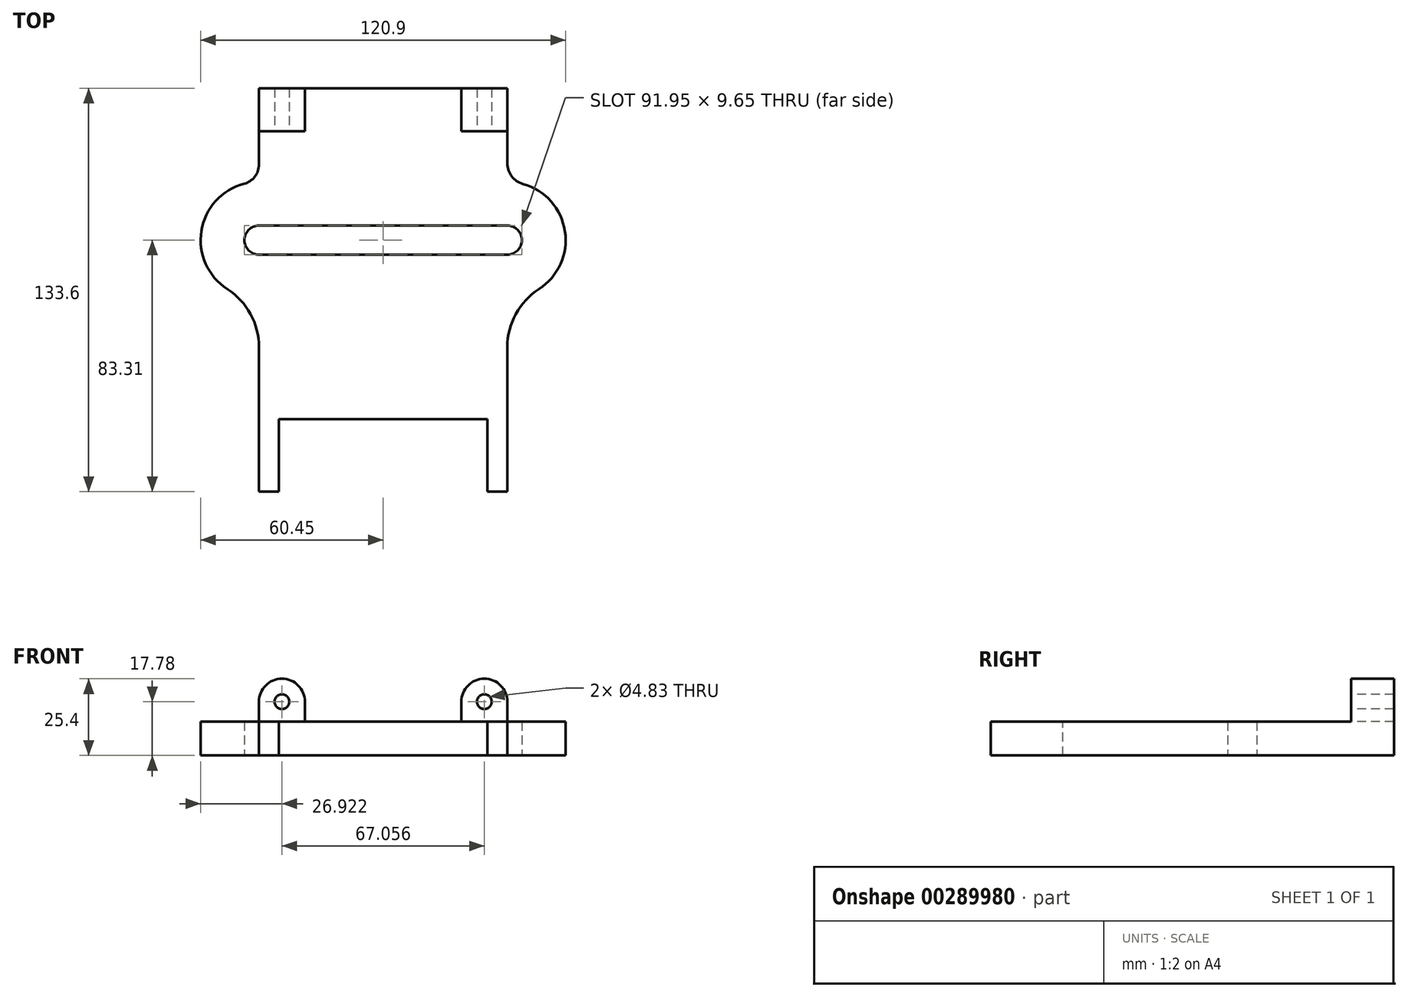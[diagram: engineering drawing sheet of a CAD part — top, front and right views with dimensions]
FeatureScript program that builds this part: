
annotation { "Feature Type Name" : "Feature", "Feature Type Description" : "" }
export const myFeature = defineFeature(function(context is Context, id is Id, definition is map)
    precondition{}
    {
        {
            var Q0;
            Q0=qCreatedBy(makeId("Top.planeOp"),FACE);
            var sketch = newSketch(context, id + "F0", { "sketchPlane" : qUnion([Q0])});
            skLineSegment(sketch, "E0.bottom", {"start": v(41.15, -66.8) * mm, "end": v(-41.15, -66.8) * mm});
            skLineSegment(sketch, "E0.top", {"start": v(41.15, 66.8) * mm, "end": v(-41.15, 66.8) * mm});
            skLineSegment(sketch, "E0.left", {"start": v(41.15, -66.8) * mm, "end": v(41.15, -18.92) * mm});
            skLineSegment(sketch, "E0.right", {"start": v(-41.15, -66.8) * mm, "end": v(-41.15, -18.92) * mm});
            skPoint(sketch, "E0.middle", {"position": v(0, 0) * mm});
            skLineSegment(sketch, "E1.bottom", {"start": v(-36.58, 66.8) * mm, "end": v(36.58, 66.8) * mm});
            skLineSegment(sketch, "E1.top", {"start": v(-36.58, -66.8) * mm, "end": v(36.58, -66.8) * mm});
            skArc(sketch, "E2", {"start": v(51.61, 0.29) * mm, "mid": v(60.23, 19.4) * mm, "end": v(46.35, 35.1) * mm});
            skArc(sketch, "E3", {"start": v(-46.07, 35.18) * mm, "mid": v(-60.21, 19.54) * mm, "end": v(-51.61, 0.29) * mm});
            skArc(sketch, "E4", {"start": v(51.61, 0.29) * mm, "mid": v(43.93, -7.98) * mm, "end": v(41.15, -18.92) * mm});
            skLineSegment(sketch, "E5.trimOffspring", {"start": v(41.15, 41.95) * mm, "end": v(41.15, 66.8) * mm});
            skArc(sketch, "E6", {"start": v(41.15, 41.95) * mm, "mid": v(42.6, 37.65) * mm, "end": v(46.35, 35.1) * mm});
            skArc(sketch, "E7", {"start": v(-41.15, -18.92) * mm, "mid": v(-43.93, -7.98) * mm, "end": v(-51.61, 0.29) * mm});
            skLineSegment(sketch, "E8.trimOffspring", {"start": v(-41.15, 41.56) * mm, "end": v(-41.15, 66.8) * mm});
            skArc(sketch, "E9", {"start": v(-46.07, 35.18) * mm, "mid": v(-42.52, 37.53) * mm, "end": v(-41.15, 41.56) * mm});
            skArc(sketch, "E10", {"start": v(-41.15, 21.34) * mm, "mid": v(-45.97, 16.5) * mm, "end": v(-41.15, 11.68) * mm});
            skArc(sketch, "E11", {"start": v(41.15, 11.68) * mm, "mid": v(45.97, 16.5) * mm, "end": v(41.15, 21.34) * mm});
            skLineSegment(sketch, "E12", {"start": v(-41.15, 21.34) * mm, "end": v(41.15, 21.34) * mm});
            skLineSegment(sketch, "E13", {"start": v(-42.2, 11.68) * mm, "end": v(41.15, 11.68) * mm});
            skSolve(sketch);
        }
        {
            var Q0;
            {var subQ3=sQuery(id+"F0.wireOp",EDGE,"E0.left");Q0=makeQuery(id+"F0.imprint","IMPRINT",FACE,{"disambiguationData":[TD([[makeQuery(id+"F0.imprint","IMPRINT",EDGE,{"derivedFrom":subQ3}),1.0]])]});}
            extrude(context, id + "F1", {"entities" : qUnion([Q0]), "depth" : 11.18 * mm});
        }
        {
            var Q0;
            Q0=makeQuery(id+"F1.opExtrude","CAP_FACE",FACE,{"disambiguationData":[OSD([sQuery(id+"F0.wireOp",EDGE,"E0.bottom"),sQuery(id+"F0.wireOp",EDGE,"E0.top"),sQuery(id+"F0.wireOp",EDGE,"E0.left"),sQuery(id+"F0.wireOp",EDGE,"E0.right"),sQuery(id+"F0.wireOp",EDGE,"E1.bottom"),sQuery(id+"F0.wireOp",EDGE,"E1.top"),sQuery(id+"F0.wireOp",EDGE,"E2"),sQuery(id+"F0.wireOp",EDGE,"E3"),sQuery(id+"F0.wireOp",EDGE,"E4"),sQuery(id+"F0.wireOp",EDGE,"E5.trimOffspring"),sQuery(id+"F0.wireOp",EDGE,"E6"),sQuery(id+"F0.wireOp",EDGE,"E7"),sQuery(id+"F0.wireOp",EDGE,"E8.trimOffspring"),sQuery(id+"F0.wireOp",EDGE,"E9"),sQuery(id+"F0.wireOp",EDGE,"E10"),sQuery(id+"F0.wireOp",EDGE,"E11"),sQuery(id+"F0.wireOp",EDGE,"E12"),sQuery(id+"F0.wireOp",EDGE,"E13")])],"isStart":false});
            var sketch = newSketch(context, id + "F2", { "sketchPlane" : qUnion([Q0])});
            skLineSegment(sketch, "E14.bottom", {"start": v(-41.15, 66.8) * mm, "end": v(-25.9, 66.8) * mm});
            skLineSegment(sketch, "E14.top", {"start": v(-41.15, 52.58) * mm, "end": v(-25.9, 52.58) * mm});
            skLineSegment(sketch, "E14.left", {"start": v(-41.15, 66.8) * mm, "end": v(-41.15, 52.58) * mm});
            skLineSegment(sketch, "E14.right", {"start": v(-25.9, 66.8) * mm, "end": v(-25.9, 52.58) * mm});
            skLineSegment(sketch, "E15.bottom", {"start": v(41.15, 66.8) * mm, "end": v(25.9, 66.8) * mm});
            skLineSegment(sketch, "E15.top", {"start": v(41.15, 52.58) * mm, "end": v(25.9, 52.58) * mm});
            skLineSegment(sketch, "E15.left", {"start": v(41.15, 66.8) * mm, "end": v(41.15, 52.58) * mm});
            skLineSegment(sketch, "E15.right", {"start": v(25.9, 66.8) * mm, "end": v(25.9, 52.58) * mm});
            skSolve(sketch);
        }
        {
            var Q0;
            Q0=makeQuery(id+"F2.imprint","IMPRINT",FACE,{"disambiguationData":[TD([[makeQuery(id+"F2.imprint","IMPRINT",EDGE,{"derivedFrom":sQuery(id+"F2.wireOp",EDGE,"E14.bottom")}),1.0]])]});
            var Q1;
            Q1=makeQuery(id+"F2.imprint","IMPRINT",FACE,{"disambiguationData":[TD([[makeQuery(id+"F2.imprint","IMPRINT",EDGE,{"derivedFrom":sQuery(id+"F2.wireOp",EDGE,"E15.bottom")}),1.0]])]});
            extrude(context, id + "F3", {"entities" : qUnion([Q0, Q1]), "operationType" : NewBodyOperationType.ADD, "depth" : 14.22 * mm});
        }
        {
            var Q0;
            Q0=makeQuery(id+"F3.opExtrude","SWEPT_FACE",FACE,{"disambiguationData":[OSD([sQuery(id+"F2.wireOp",EDGE,"E14.top")])]});
            var sketch = newSketch(context, id + "F4", { "sketchPlane" : qUnion([Q0])});
            skCircle(sketch, "E16", {"center": v(-33.53, 17.78) * mm, "radius": 2.41 * mm});
            skCircle(sketch, "E17", {"center": v(33.53, 17.78) * mm, "radius": 2.41 * mm});
            skSolve(sketch);
        }
        {
            var Q0;
            Q0=makeQuery(id+"F4.imprint","IMPRINT",FACE,{"disambiguationData":[TD([[makeQuery(id+"F4.imprint","IMPRINT",EDGE,{"derivedFrom":sQuery(id+"F4.wireOp",EDGE,"E16")}),1.0]])]});
            var Q1;
            Q1=makeQuery(id+"F4.imprint","IMPRINT",FACE,{"disambiguationData":[TD([[makeQuery(id+"F4.imprint","IMPRINT",EDGE,{"derivedFrom":sQuery(id+"F4.wireOp",EDGE,"E17")}),1.0]])]});
            extrude(context, id + "F5", {"entities" : qUnion([Q0, Q1]), "operationType" : NewBodyOperationType.REMOVE, "endBound" : BoundingType.THROUGH_ALL, "oppositeDirection" : true, "depth" : 25.4 * mm});
        }
        {
            var Q0;
            Q0=makeQuery(id+"F3.opExtrude","SWEPT_FACE",FACE,{"disambiguationData":[OSD([sQuery(id+"F2.wireOp",EDGE,"E15.top")])]});
            var sketch = newSketch(context, id + "F6", { "sketchPlane" : qUnion([Q0])});
            skCircle(sketch, "E18", {"center": v(33.53, 17.78) * mm, "radius": 7.62 * mm});
            skSolve(sketch);
        }
        {
            var Q0;
            {var subQ0=sQuery(id+"F6.wireOp",EDGE,"E18");var subQ1=sQuery(id+"F2.wireOp",EDGE,"E15.top");var subQ2=makeQuery(id+"F3.opExtrude","CAP_EDGE",EDGE,{"disambiguationData":[OSD([subQ1])],"isStart":false});var subQ3=makeQuery(id+"F6.imprint","INTERSECT",VERTEX,{"derivedFrom":[subQ2,subQ0]});Q0=makeQuery(id+"F6.imprint","IMPRINT",FACE,{"disambiguationData":[TD([[makeQuery(id+"F6.imprint","IMPRINT",EDGE,{"disambiguationData":[TD([[subQ3,1.0]])],"derivedFrom":subQ0}),-1.0]])]});}
            var Q1;
            {var subQ0=sQuery(id+"F6.wireOp",EDGE,"E18");var subQ1=sQuery(id+"F2.wireOp",EDGE,"E15.top");var subQ2=makeQuery(id+"F3.opExtrude","CAP_EDGE",EDGE,{"disambiguationData":[OSD([subQ1])],"isStart":false});var subQ3=makeQuery(id+"F6.imprint","INTERSECT",VERTEX,{"derivedFrom":[subQ2,subQ0]});Q1=makeQuery(id+"F6.imprint","IMPRINT",FACE,{"disambiguationData":[TD([[makeQuery(id+"F6.imprint","IMPRINT",EDGE,{"disambiguationData":[TD([[subQ3,-1.0]])],"derivedFrom":subQ0}),-1.0]])]});}
            extrude(context, id + "F7", {"entities" : qUnion([Q0, Q1]), "operationType" : NewBodyOperationType.REMOVE, "endBound" : BoundingType.THROUGH_ALL, "oppositeDirection" : true, "depth" : 25.4 * mm});
        }
        {
            var Q0;
            Q0=makeQuery(id+"F3.opExtrude","SWEPT_FACE",FACE,{"disambiguationData":[OSD([sQuery(id+"F2.wireOp",EDGE,"E14.top")])]});
            var sketch = newSketch(context, id + "F8", { "sketchPlane" : qUnion([Q0])});
            skCircle(sketch, "E19", {"center": v(-33.53, 17.78) * mm, "radius": 7.62 * mm});
            skSolve(sketch);
        }
        {
            var Q0;
            {var subQ0=sQuery(id+"F8.wireOp",EDGE,"E19");var subQ1=sQuery(id+"F2.wireOp",EDGE,"E14.top");var subQ2=makeQuery(id+"F3.opExtrude","CAP_EDGE",EDGE,{"disambiguationData":[OSD([subQ1])],"isStart":false});var subQ3=makeQuery(id+"F8.imprint","INTERSECT",VERTEX,{"derivedFrom":[subQ2,subQ0]});Q0=makeQuery(id+"F8.imprint","IMPRINT",FACE,{"disambiguationData":[TD([[makeQuery(id+"F8.imprint","IMPRINT",EDGE,{"disambiguationData":[TD([[subQ3,-1.0]])],"derivedFrom":subQ0}),-1.0]])]});}
            var Q1;
            {var subQ0=sQuery(id+"F8.wireOp",EDGE,"E19");var subQ1=sQuery(id+"F2.wireOp",EDGE,"E14.top");var subQ2=makeQuery(id+"F3.opExtrude","CAP_EDGE",EDGE,{"disambiguationData":[OSD([subQ1])],"isStart":false});var subQ3=makeQuery(id+"F8.imprint","INTERSECT",VERTEX,{"derivedFrom":[subQ2,subQ0]});Q1=makeQuery(id+"F8.imprint","IMPRINT",FACE,{"disambiguationData":[TD([[makeQuery(id+"F8.imprint","IMPRINT",EDGE,{"disambiguationData":[TD([[subQ3,1.0]])],"derivedFrom":subQ0}),-1.0]])]});}
            extrude(context, id + "F9", {"entities" : qUnion([Q0, Q1]), "operationType" : NewBodyOperationType.REMOVE, "endBound" : BoundingType.THROUGH_ALL, "oppositeDirection" : true, "depth" : 25.4 * mm});
        }
        {
            var Q0;
            Q0=makeQuery(id+"F1.opExtrude","CAP_FACE",FACE,{"disambiguationData":[OSD([sQuery(id+"F0.wireOp",EDGE,"E0.bottom"),sQuery(id+"F0.wireOp",EDGE,"E0.top"),sQuery(id+"F0.wireOp",EDGE,"E0.left"),sQuery(id+"F0.wireOp",EDGE,"E0.right"),sQuery(id+"F0.wireOp",EDGE,"E1.bottom"),sQuery(id+"F0.wireOp",EDGE,"E1.top"),sQuery(id+"F0.wireOp",EDGE,"E2"),sQuery(id+"F0.wireOp",EDGE,"E3"),sQuery(id+"F0.wireOp",EDGE,"E4"),sQuery(id+"F0.wireOp",EDGE,"E5.trimOffspring"),sQuery(id+"F0.wireOp",EDGE,"E6"),sQuery(id+"F0.wireOp",EDGE,"E7"),sQuery(id+"F0.wireOp",EDGE,"E8.trimOffspring"),sQuery(id+"F0.wireOp",EDGE,"E9"),sQuery(id+"F0.wireOp",EDGE,"E10"),sQuery(id+"F0.wireOp",EDGE,"E11"),sQuery(id+"F0.wireOp",EDGE,"E12"),sQuery(id+"F0.wireOp",EDGE,"E13")])],"isStart":false});
            var sketch = newSketch(context, id + "F10", { "sketchPlane" : qUnion([Q0])});
            skLineSegment(sketch, "E20", {"start": v(-34.54, -42.86) * mm, "end": v(34.54, -42.86) * mm});
            skPoint(sketch, "E20.startSnap0", {"position": v(-41.15, -42.86) * mm});
            skLineSegment(sketch, "E21", {"start": v(-34.54, -42.86) * mm, "end": v(-34.54, -66.8) * mm});
            skLineSegment(sketch, "E22", {"start": v(34.54, -42.86) * mm, "end": v(34.54, -66.8) * mm});
            skSolve(sketch);
        }
        {
            var Q0;
            Q0=makeQuery(id+"F10.imprint","IMPRINT",FACE,{"disambiguationData":[TD([[makeQuery(id+"F10.imprint","IMPRINT",EDGE,{"derivedFrom":sQuery(id+"F10.wireOp",EDGE,"E20")}),-1.0]])]});
            extrude(context, id + "F11", {"entities" : qUnion([Q0]), "operationType" : NewBodyOperationType.REMOVE, "endBound" : BoundingType.THROUGH_ALL, "oppositeDirection" : true, "depth" : 25.4 * mm});
        }
    });
